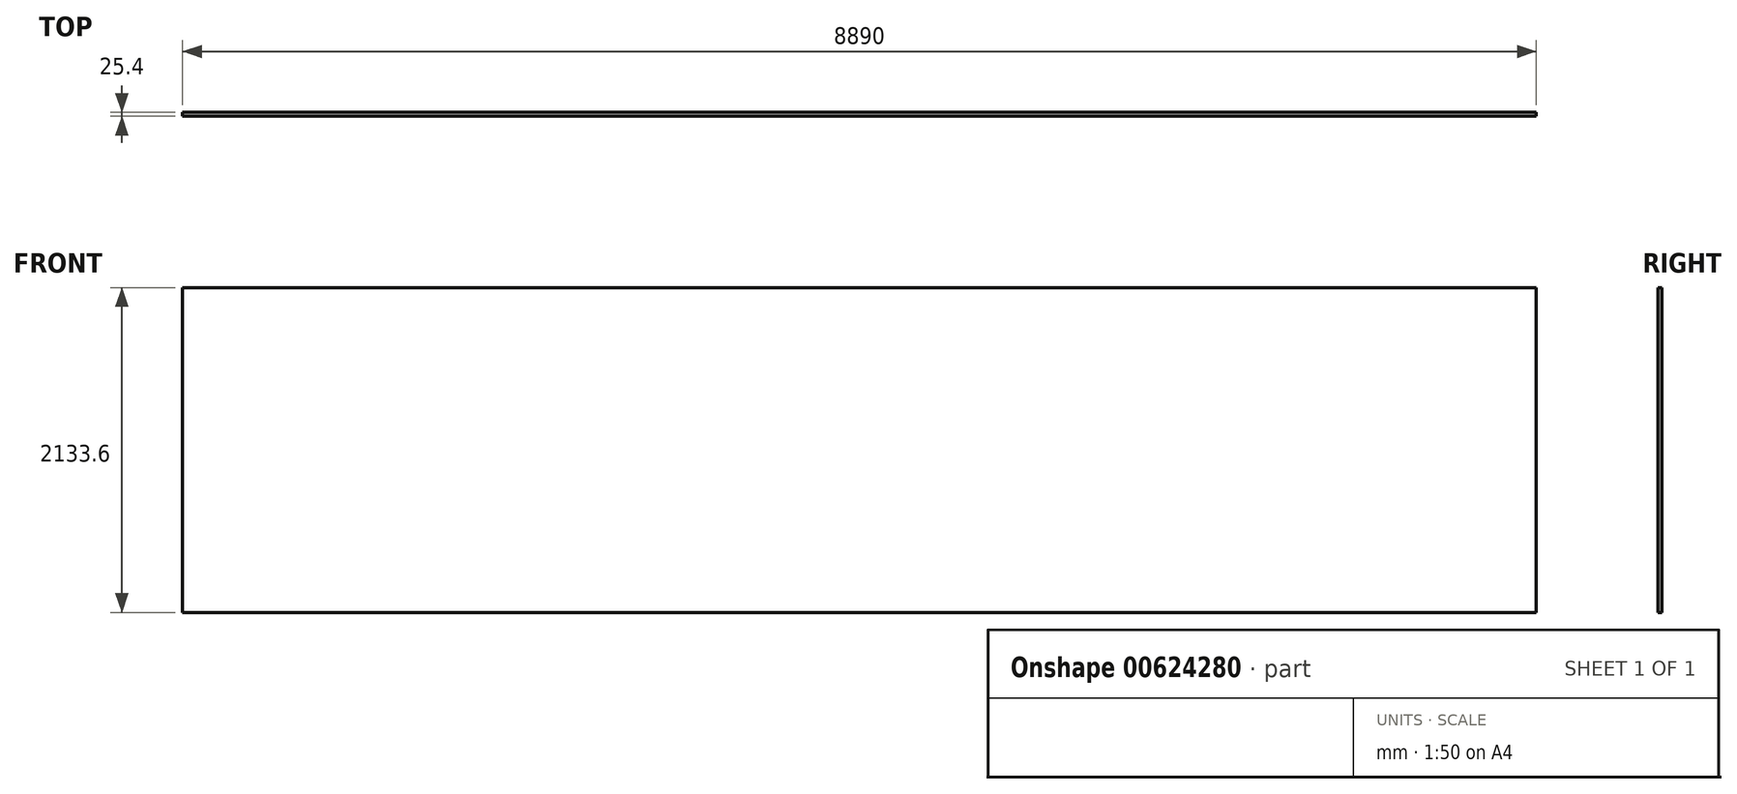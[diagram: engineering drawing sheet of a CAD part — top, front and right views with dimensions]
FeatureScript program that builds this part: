
annotation { "Feature Type Name" : "Feature", "Feature Type Description" : "" }
export const myFeature = defineFeature(function(context is Context, id is Id, definition is map)
    precondition{}
    {
        {
            var Q0;
            Q0=qCreatedBy(makeId("Front.planeOp"),FACE);
            var sketch = newSketch(context, id + "F0", { "sketchPlane" : qUnion([Q0])});
            skLineSegment(sketch, "E0.bottom", {"start": v(0, 0) * mm, "end": v(8890, 0) * mm});
            skLineSegment(sketch, "E0.top", {"start": v(0, -2133.6) * mm, "end": v(8890, -2133.6) * mm});
            skLineSegment(sketch, "E0.left", {"start": v(0, 0) * mm, "end": v(0, -2133.6) * mm});
            skLineSegment(sketch, "E0.right", {"start": v(8890, 0) * mm, "end": v(8890, -2133.6) * mm});
            skSolve(sketch);
        }
        {
            var Q0;
            Q0 = qSketchRegion(id + "F0", true);
            extrude(context, id + "F1", {"entities" : qUnion([Q0]), "depth" : 25.4 * mm, "offsetDistance" : 25.4 * mm});
        }
    });
